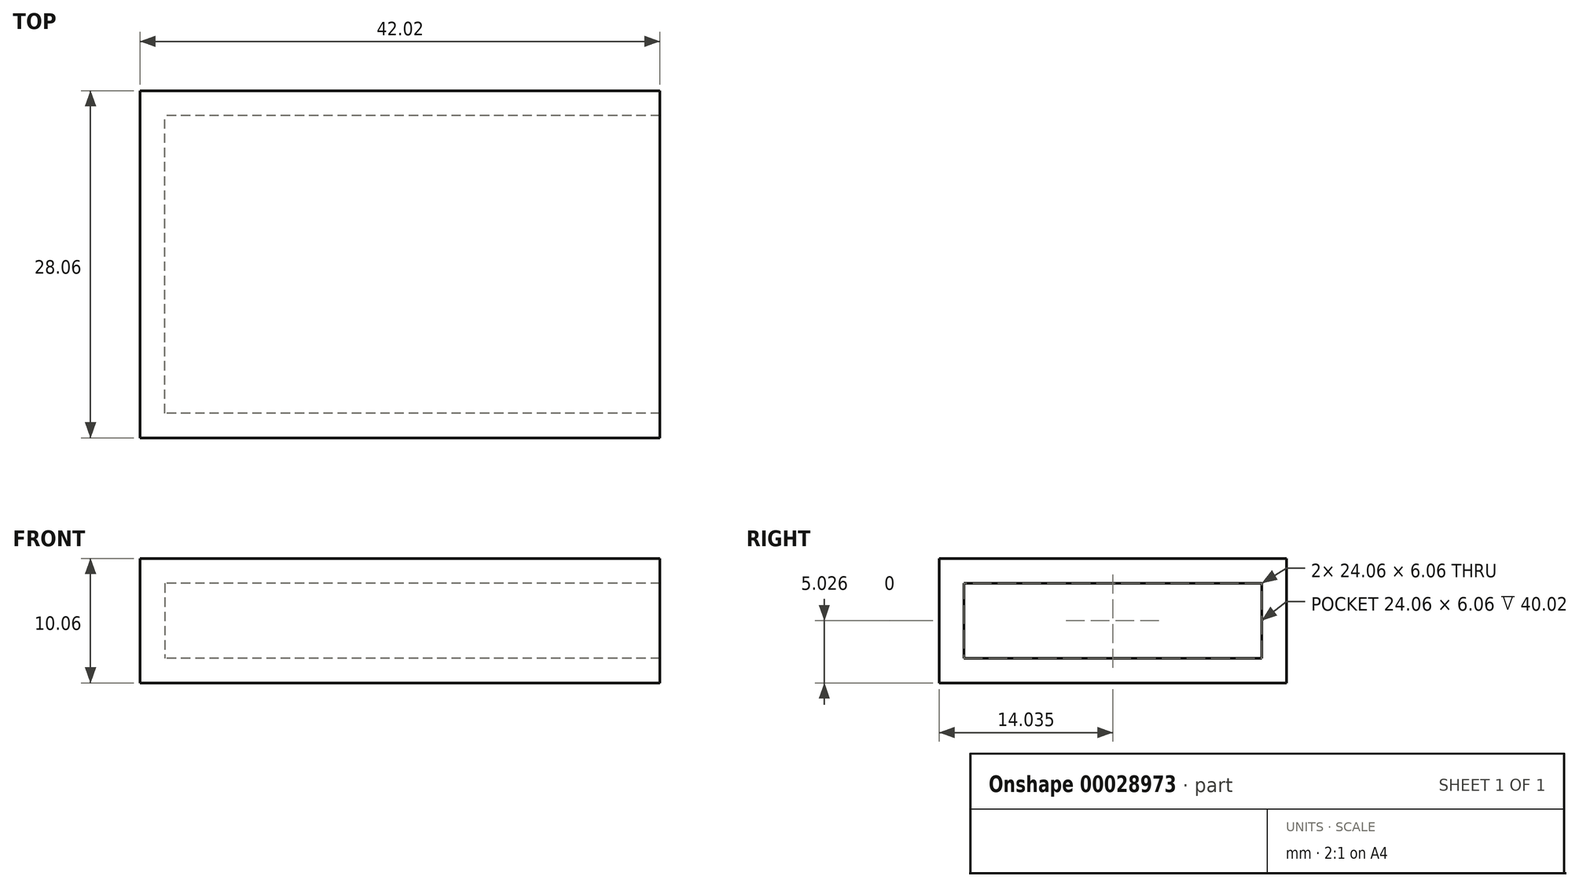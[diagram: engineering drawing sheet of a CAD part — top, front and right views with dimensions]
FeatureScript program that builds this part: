
annotation { "Feature Type Name" : "Feature", "Feature Type Description" : "" }
export const myFeature = defineFeature(function(context is Context, id is Id, definition is map)
    precondition{}
    {
        {
            var Q0;
            Q0=qCreatedBy(makeId("Right.planeOp"),FACE);
            var sketch = newSketch(context, id + "F0", { "sketchPlane" : qUnion([Q0])});
            skLineSegment(sketch, "E0.bottom", {"start": v(-17.02, 23.49) * mm, "end": v(11.04, 23.49) * mm});
            skLineSegment(sketch, "E0.top", {"start": v(-17.02, 13.43) * mm, "end": v(11.04, 13.43) * mm});
            skLineSegment(sketch, "E0.left", {"start": v(-17.02, 23.49) * mm, "end": v(-17.02, 13.43) * mm});
            skLineSegment(sketch, "E0.right", {"start": v(11.04, 23.49) * mm, "end": v(11.04, 13.43) * mm});
            skSolve(sketch);
        }
        {
            var Q0;
            Q0=makeQuery(id+"F0.imprint","IMPRINT",FACE,{"disambiguationData":[TD([[makeQuery(id+"F0.imprint","IMPRINT",EDGE,{"derivedFrom":sQuery(id+"F0.wireOp",EDGE,"E0.bottom")}),-1.0]])]});
            extrude(context, id + "F1", {"entities" : qUnion([Q0]), "depth" : 42.02 * mm});
        }
        {
            var Q0;
            Q0=makeQuery(id+"F1.opExtrude","CAP_FACE",FACE,{"disambiguationData":[OSD([sQuery(id+"F0.wireOp",EDGE,"E0.bottom"),sQuery(id+"F0.wireOp",EDGE,"E0.top"),sQuery(id+"F0.wireOp",EDGE,"E0.left"),sQuery(id+"F0.wireOp",EDGE,"E0.right")])],"isStart":false});
            shell(context, id + "F2", {"entities" : qUnion([Q0]), "thickness" : 2 * mm});
        }
    });
